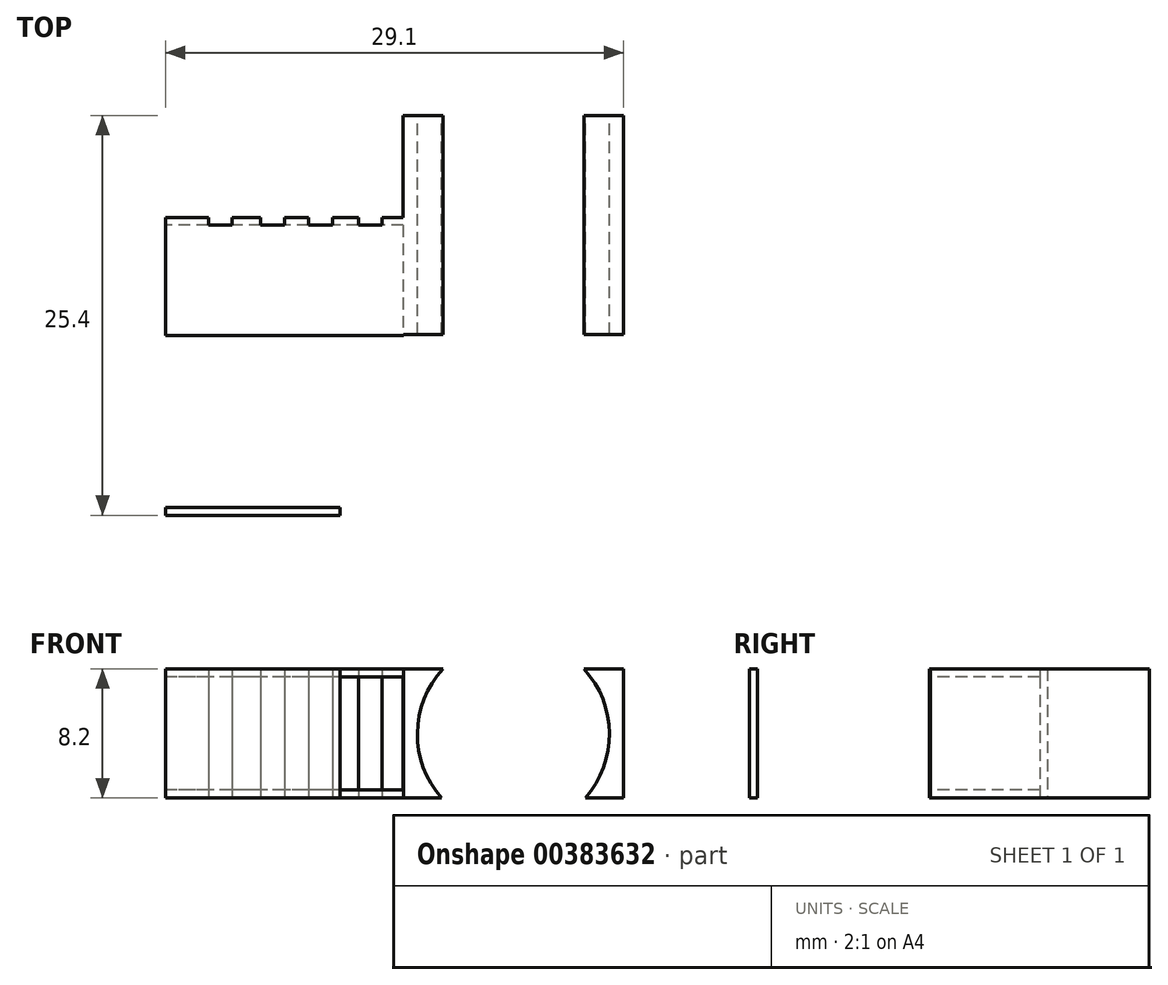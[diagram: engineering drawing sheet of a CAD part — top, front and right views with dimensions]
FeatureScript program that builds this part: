
annotation { "Feature Type Name" : "Feature", "Feature Type Description" : "" }
export const myFeature = defineFeature(function(context is Context, id is Id, definition is map)
    precondition{}
    {
        {
            var Q0;
            Q0=qCreatedBy(makeId("Top.planeOp"),FACE);
            var sketch = newSketch(context, id + "F0", { "sketchPlane" : qUnion([Q0])});
            skLineSegment(sketch, "E0.bottom", {"start": v(0, 0) * mm, "end": v(29.1, 0) * mm});
            skLineSegment(sketch, "E0.top", {"start": v(0, 11.4) * mm, "end": v(29.1, 11.4) * mm});
            skLineSegment(sketch, "E0.left", {"start": v(0, 0) * mm, "end": v(0, 11.4) * mm});
            skLineSegment(sketch, "E0.right", {"start": v(29.1, 0) * mm, "end": v(29.1, 11.4) * mm});
            skLineSegment(sketch, "E1.bottom", {"start": v(29.1, 11.4) * mm, "end": v(15.1, 11.4) * mm});
            skLineSegment(sketch, "E1.top", {"start": v(29.1, 25.4) * mm, "end": v(15.1, 25.4) * mm});
            skLineSegment(sketch, "E1.left", {"start": v(29.1, 11.4) * mm, "end": v(29.1, 25.4) * mm});
            skLineSegment(sketch, "E1.right", {"start": v(15.1, 11.4) * mm, "end": v(15.1, 25.4) * mm});
            skSolve(sketch);
        }
        {
            var Q0;
            Q0=qSketchRegion(id+"F0",true);
            extrude(context, id + "F1", {"entities" : qUnion([Q0]), "depth" : 8.2 * mm});
        }
        {
            var Q0;
            Q0=makeQuery(id+"F1.opExtrude","SWEPT_FACE",FACE,{"disambiguationData":[OSD([sQuery(id+"F0.wireOp",EDGE,"E0.bottom")])]});
            var sketch = newSketch(context, id + "F2", { "sketchPlane" : qUnion([Q0])});
            skLineSegment(sketch, "E2.bottom", {"start": v(29.1, 8.2) * mm, "end": v(11.1, 8.2) * mm});
            skLineSegment(sketch, "E2.top", {"start": v(29.1, 0) * mm, "end": v(11.1, 0) * mm});
            skLineSegment(sketch, "E2.left", {"start": v(29.1, 8.2) * mm, "end": v(29.1, 0) * mm});
            skLineSegment(sketch, "E2.right", {"start": v(11.1, 8.2) * mm, "end": v(11.1, 0) * mm});
            skLineSegment(sketch, "E3.bottom", {"start": v(11.1, 0) * mm, "end": v(29.1, 0) * mm});
            skLineSegment(sketch, "E3.top", {"start": v(11.1, 0.5) * mm, "end": v(29.1, 0.5) * mm});
            skLineSegment(sketch, "E3.left", {"start": v(11.1, 0) * mm, "end": v(11.1, 0.5) * mm});
            skLineSegment(sketch, "E3.right", {"start": v(29.1, 0) * mm, "end": v(29.1, 0.5) * mm});
            skLineSegment(sketch, "E4.bottom", {"start": v(11.1, 8.2) * mm, "end": v(29.1, 8.2) * mm});
            skLineSegment(sketch, "E4.top", {"start": v(11.1, 7.7) * mm, "end": v(29.1, 7.7) * mm});
            skLineSegment(sketch, "E4.left", {"start": v(11.1, 8.2) * mm, "end": v(11.1, 7.7) * mm});
            skLineSegment(sketch, "E4.right", {"start": v(29.1, 8.2) * mm, "end": v(29.1, 7.7) * mm});
            skSolve(sketch);
        }
        {
            var Q0;
            Q0=makeQuery(id+"F2.imprint","IMPRINT",FACE,{"disambiguationData":[TD([[makeQuery(id+"F2.imprint","IMPRINT",EDGE,{"derivedFrom":sQuery(id+"F2.wireOp",EDGE,"E2.left")}),-1.0]])]});
            extrude(context, id + "F3", {"entities" : qUnion([Q0]), "operationType" : NewBodyOperationType.REMOVE, "oppositeDirection" : true, "depth" : 11.5 * mm});
        }
        {
            var Q0;
            Q0=makeQuery(id+"F1.opExtrude","SWEPT_FACE",FACE,{"disambiguationData":[OSD([sQuery(id+"F0.wireOp",EDGE,"E1.top")])]});
            var sketch = newSketch(context, id + "F4", { "sketchPlane" : qUnion([Q0])});
            skCircle(sketch, "E5", {"center": v(-22.1, 4.05) * mm, "radius": 6.1 * mm});
            skSolve(sketch);
        }
        {
            var Q0;
            {var subQ0=sQuery(id+"F4.wireOp",EDGE,"E5");var subQ1=sQuery(id+"F0.wireOp",EDGE,"E1.top");var subQ2=makeQuery(id+"F1.opExtrude","CAP_EDGE",EDGE,{"disambiguationData":[OSD([subQ1])],"isStart":false});var subQ3=makeQuery(id+"F4.imprint","INTERSECT",VERTEX,{"disambiguationData":[OD(0.0)],"derivedFrom":[subQ2,subQ0]});Q0=makeQuery(id+"F4.imprint","IMPRINT",FACE,{"disambiguationData":[TD([[makeQuery(id+"F4.imprint","IMPRINT",EDGE,{"disambiguationData":[TD([[subQ3,-1.0]])],"derivedFrom":subQ0}),1.0]])]});}
            extrude(context, id + "F5", {"entities" : qUnion([Q0]), "operationType" : NewBodyOperationType.REMOVE, "oppositeDirection" : true, "depth" : 14 * mm});
        }
        {
            var Q0;
            Q0=makeQuery(id+"F1.opExtrude","SWEPT_FACE",FACE,{"disambiguationData":[OSD([sQuery(id+"F0.wireOp",EDGE,"E0.left")])]});
            var sketch = newSketch(context, id + "F6", { "sketchPlane" : qUnion([Q0])});
            skLineSegment(sketch, "E6.bottom", {"start": v(0, 8.2) * mm, "end": v(-0.5, 8.2) * mm});
            skLineSegment(sketch, "E6.top", {"start": v(0, 0) * mm, "end": v(-0.5, 0) * mm});
            skLineSegment(sketch, "E6.left", {"start": v(0, 8.2) * mm, "end": v(0, 0) * mm});
            skLineSegment(sketch, "E6.right", {"start": v(-0.5, 8.2) * mm, "end": v(-0.5, 0) * mm});
            skLineSegment(sketch, "E7.bottom", {"start": v(-11.4, 8.2) * mm, "end": v(-0.5, 8.2) * mm});
            skLineSegment(sketch, "E7.top", {"start": v(-11.4, 7.7) * mm, "end": v(-0.5, 7.7) * mm});
            skLineSegment(sketch, "E7.left", {"start": v(-11.4, 8.2) * mm, "end": v(-11.4, 7.7) * mm});
            skLineSegment(sketch, "E7.right", {"start": v(-0.5, 8.2) * mm, "end": v(-0.5, 7.7) * mm});
            skLineSegment(sketch, "E8.bottom", {"start": v(-11.4, 0) * mm, "end": v(-0.5, 0) * mm});
            skLineSegment(sketch, "E8.top", {"start": v(-11.4, 0.5) * mm, "end": v(-0.5, 0.5) * mm});
            skLineSegment(sketch, "E8.left", {"start": v(-11.4, 0) * mm, "end": v(-11.4, 0.5) * mm});
            skLineSegment(sketch, "E8.right", {"start": v(-0.5, 0) * mm, "end": v(-0.5, 0.5) * mm});
            skSolve(sketch);
        }
        {
            var Q0;
            {var subQ0=sQuery(id+"F6.wireOp",EDGE,"E6.right");Q0=makeQuery(id+"F6.imprint","IMPRINT",FACE,{"disambiguationData":[TD([[makeQuery(id+"F6.imprint","IMPRINT",EDGE,{"derivedFrom":subQ0}),-1.0]])]});}
            extrude(context, id + "F7", {"entities" : qUnion([Q0]), "operationType" : NewBodyOperationType.REMOVE, "oppositeDirection" : true, "depth" : 25 * mm});
        }
        {
            var Q0;
            Q0=qCreatedBy(makeId("Top.planeOp"),FACE);
            var sketch = newSketch(context, id + "F8", { "sketchPlane" : qUnion([Q0])});
            skLineSegment(sketch, "E9.bottom", {"start": v(0, 11.41) * mm, "end": v(15.1, 11.41) * mm});
            skLineSegment(sketch, "E9.top", {"start": v(0, 18.93) * mm, "end": v(15.1, 18.93) * mm});
            skLineSegment(sketch, "E9.left", {"start": v(0, 11.41) * mm, "end": v(0, 18.93) * mm});
            skLineSegment(sketch, "E9.right", {"start": v(15.1, 11.41) * mm, "end": v(15.1, 18.93) * mm});
            skSolve(sketch);
        }
        {
            var Q0;
            Q0=makeQuery(id+"F8.imprint","IMPRINT",FACE,{"disambiguationData":[TD([[makeQuery(id+"F8.imprint","IMPRINT",EDGE,{"derivedFrom":sQuery(id+"F8.wireOp",EDGE,"E9.bottom")}),1.0]])]});
            var Q1;
            Q1 = qSketchRegion(id + "F8", true);
            extrude(context, id + "F9", {"entities" : qUnion([Q0, Q1]), "operationType" : NewBodyOperationType.ADD, "depth" : 8.2 * mm});
        }
        {
            var Q0;
            Q0=makeQuery(id+"F9.opExtrude","SWEPT_FACE",FACE,{"disambiguationData":[OSD([sQuery(id+"F8.wireOp",EDGE,"E9.left")])]});
            var sketch = newSketch(context, id + "F10", { "sketchPlane" : qUnion([Q0])});
            skLineSegment(sketch, "E10.bottom", {"start": v(-18.93, 0) * mm, "end": v(-18.43, 0) * mm});
            skLineSegment(sketch, "E10.top", {"start": v(-18.93, 8.2) * mm, "end": v(-18.43, 8.2) * mm});
            skLineSegment(sketch, "E10.left", {"start": v(-18.93, 0) * mm, "end": v(-18.93, 8.2) * mm});
            skLineSegment(sketch, "E10.right", {"start": v(-18.43, 0) * mm, "end": v(-18.43, 8.2) * mm});
            skLineSegment(sketch, "E11.bottom", {"start": v(-18.93, 8.2) * mm, "end": v(-11.41, 8.2) * mm});
            skLineSegment(sketch, "E11.top", {"start": v(-18.93, 7.7) * mm, "end": v(-11.41, 7.7) * mm});
            skLineSegment(sketch, "E11.left", {"start": v(-18.93, 8.2) * mm, "end": v(-18.93, 7.7) * mm});
            skLineSegment(sketch, "E11.right", {"start": v(-11.41, 8.2) * mm, "end": v(-11.41, 7.7) * mm});
            skLineSegment(sketch, "E12.bottom", {"start": v(-18.93, 0) * mm, "end": v(-11.41, 0) * mm});
            skLineSegment(sketch, "E12.top", {"start": v(-18.93, 0.5) * mm, "end": v(-11.41, 0.5) * mm});
            skLineSegment(sketch, "E12.left", {"start": v(-18.93, 0) * mm, "end": v(-18.93, 0.5) * mm});
            skLineSegment(sketch, "E12.right", {"start": v(-11.41, 0) * mm, "end": v(-11.41, 0.5) * mm});
            skSolve(sketch);
        }
        {
            var Q0;
            {var subQ0=sQuery(id+"F10.wireOp",EDGE,"E12.top");var subQ1=sQuery(id+"F10.wireOp",EDGE,"E10.right");var subQ2=makeQuery(id+"F10.imprint","INTERSECT",VERTEX,{"derivedFrom":[subQ1,subQ0]});Q0=makeQuery(id+"F10.imprint","IMPRINT",FACE,{"disambiguationData":[TD([[makeQuery(id+"F10.imprint","IMPRINT",EDGE,{"disambiguationData":[TD([[subQ2,-1.0]])],"derivedFrom":subQ1}),-1.0]])]});}
            extrude(context, id + "F11", {"entities" : qUnion([Q0]), "operationType" : NewBodyOperationType.REMOVE, "oppositeDirection" : true, "depth" : 15.1 * mm});
        }
        {
            var Q0;
            Q0=makeQuery(id+"F9.opExtrude","SWEPT_FACE",FACE,{"disambiguationData":[OSD([sQuery(id+"F8.wireOp",EDGE,"E9.top")])]});
            var sketch = newSketch(context, id + "F12", { "sketchPlane" : qUnion([Q0])});
            skLineSegment(sketch, "E13.bottom", {"start": v(-13.76, 8.2) * mm, "end": v(-12.26, 8.2) * mm});
            skLineSegment(sketch, "E13.top", {"start": v(-13.76, 0) * mm, "end": v(-12.26, 0) * mm});
            skLineSegment(sketch, "E13.left", {"start": v(-13.76, 8.2) * mm, "end": v(-13.76, 0) * mm});
            skLineSegment(sketch, "E13.right", {"start": v(-12.26, 8.2) * mm, "end": v(-12.26, 0) * mm});
            skLineSegment(sketch, "E14.bottom", {"start": v(-10.6, 8.2) * mm, "end": v(-9.1, 8.2) * mm});
            skLineSegment(sketch, "E14.top", {"start": v(-10.6, 0) * mm, "end": v(-9.1, 0) * mm});
            skLineSegment(sketch, "E14.left", {"start": v(-10.6, 8.2) * mm, "end": v(-10.6, 0) * mm});
            skLineSegment(sketch, "E14.right", {"start": v(-9.1, 8.2) * mm, "end": v(-9.1, 0) * mm});
            skLineSegment(sketch, "E15.bottom", {"start": v(-7.55, 8.2) * mm, "end": v(-6.05, 8.2) * mm});
            skLineSegment(sketch, "E15.top", {"start": v(-7.55, 0) * mm, "end": v(-6.05, 0) * mm});
            skLineSegment(sketch, "E15.left", {"start": v(-7.55, 8.2) * mm, "end": v(-7.55, 0) * mm});
            skLineSegment(sketch, "E15.right", {"start": v(-6.05, 8.2) * mm, "end": v(-6.05, 0) * mm});
            skLineSegment(sketch, "E16.bottom", {"start": v(-4.23, 8.2) * mm, "end": v(-2.73, 8.2) * mm});
            skLineSegment(sketch, "E16.top", {"start": v(-4.23, 0) * mm, "end": v(-2.73, 0) * mm});
            skLineSegment(sketch, "E16.left", {"start": v(-4.23, 8.2) * mm, "end": v(-4.23, 0) * mm});
            skLineSegment(sketch, "E16.right", {"start": v(-2.73, 8.2) * mm, "end": v(-2.73, 0) * mm});
            skSolve(sketch);
        }
        {
            var Q0;
            Q0=makeQuery(id+"F12.imprint","IMPRINT",FACE,{"disambiguationData":[TD([[makeQuery(id+"F12.imprint","IMPRINT",EDGE,{"derivedFrom":sQuery(id+"F12.wireOp",EDGE,"E13.bottom")}),1.0]])]});
            var Q1;
            Q1=makeQuery(id+"F12.imprint","IMPRINT",FACE,{"disambiguationData":[TD([[makeQuery(id+"F12.imprint","IMPRINT",EDGE,{"derivedFrom":sQuery(id+"F12.wireOp",EDGE,"E15.bottom")}),1.0]])]});
            var Q2;
            Q2=makeQuery(id+"F12.imprint","IMPRINT",FACE,{"disambiguationData":[TD([[makeQuery(id+"F12.imprint","IMPRINT",EDGE,{"derivedFrom":sQuery(id+"F12.wireOp",EDGE,"E14.bottom")}),1.0]])]});
            var Q3;
            Q3=makeQuery(id+"F12.imprint","IMPRINT",FACE,{"disambiguationData":[TD([[makeQuery(id+"F12.imprint","IMPRINT",EDGE,{"derivedFrom":sQuery(id+"F12.wireOp",EDGE,"E16.bottom")}),1.0]])]});
            extrude(context, id + "F13", {"entities" : qUnion([Q0, Q1, Q2, Q3]), "operationType" : NewBodyOperationType.REMOVE, "oppositeDirection" : true, "depth" : 0.5 * mm});
        }
    });
